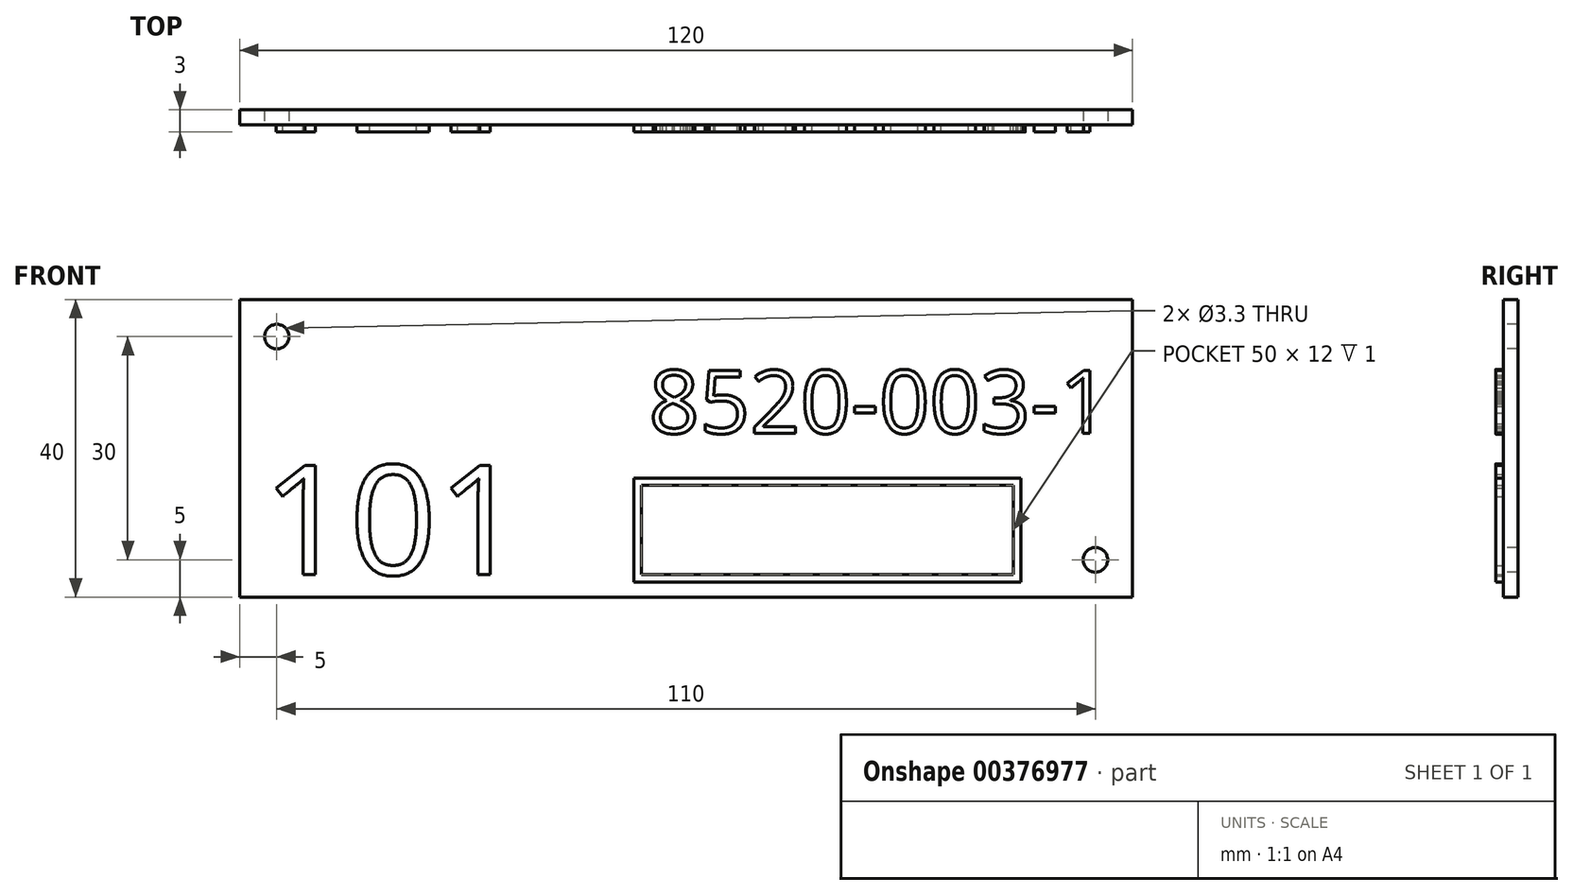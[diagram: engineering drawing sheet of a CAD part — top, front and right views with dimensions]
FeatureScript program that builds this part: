
annotation { "Feature Type Name" : "Feature", "Feature Type Description" : "" }
export const myFeature = defineFeature(function(context is Context, id is Id, definition is map)
    precondition{}
    {
        {
            var Q0;
            Q0=qCreatedBy(makeId("Front.planeOp"),FACE);
            var sketch = newSketch(context, id + "F0", { "sketchPlane" : qUnion([Q0])});
            skLineSegment(sketch, "E0.bottom", {"start": v(60, -20) * mm, "end": v(-60, -20) * mm});
            skLineSegment(sketch, "E0.top", {"start": v(60, 20) * mm, "end": v(-60, 20) * mm});
            skLineSegment(sketch, "E0.left", {"start": v(60, -20) * mm, "end": v(60, 20) * mm});
            skLineSegment(sketch, "E0.right", {"start": v(-60, -20) * mm, "end": v(-60, 20) * mm});
            skPoint(sketch, "E0.middle", {"position": v(0, 0) * mm});
            skSolve(sketch);
        }
        {
            var Q0;
            Q0=makeQuery(id+"F0.imprint","IMPRINT",FACE,{"disambiguationData":[TD([[makeQuery(id+"F0.imprint","IMPRINT",EDGE,{"derivedFrom":sQuery(id+"F0.wireOp",EDGE,"E0.bottom")}),-1.0]])]});
            extrude(context, id + "F1", {"entities" : qUnion([Q0]), "depth" : 2 * mm});
        }
        {
            var Q0;
            Q0=makeQuery(id+"F1.opExtrude","CAP_FACE",FACE,{"disambiguationData":[OSD([sQuery(id+"F0.wireOp",EDGE,"E0.bottom"),sQuery(id+"F0.wireOp",EDGE,"E0.top"),sQuery(id+"F0.wireOp",EDGE,"E0.left"),sQuery(id+"F0.wireOp",EDGE,"E0.right")])],"isStart":false});
            var sketch = newSketch(context, id + "F2", { "sketchPlane" : qUnion([Q0])});
            skPoint(sketch, "E1", {"position": v(-55, 15) * mm});
            skPoint(sketch, "E2", {"position": v(55, -15) * mm});
            skSolve(sketch);
        }
        {
            var Q0;
            Q0=sQuery(id+"F2.wireOp",VERTEX,"E1");
            var Q1;
            Q1=sQuery(id+"F2.wireOp",VERTEX,"E2");
            var Q2;
            Q2=makeQuery(id+"F1.opExtrude","SWEPT_BODY",BODY,{"disambiguationData":[OSD([sQuery(id+"F0.wireOp",EDGE,"E0.bottom"),sQuery(id+"F0.wireOp",EDGE,"E0.top"),sQuery(id+"F0.wireOp",EDGE,"E0.left"),sQuery(id+"F0.wireOp",EDGE,"E0.right")])]});
            hole(context, id + "F3", {"style" : HoleStyle.SIMPLE, "endStyle" : HoleEndStyle.THROUGH, "holeDiameter" : 3.3 * mm, "locations" : qUnion([Q0, Q1]), "scope" : qUnion([Q2]), "isTappedThrough" : true});
        }
        {
            var Q0;
            Q0=makeQuery(id+"F1.opExtrude","CAP_FACE",FACE,{"disambiguationData":[OSD([sQuery(id+"F0.wireOp",EDGE,"E0.bottom"),sQuery(id+"F0.wireOp",EDGE,"E0.top"),sQuery(id+"F0.wireOp",EDGE,"E0.left"),sQuery(id+"F0.wireOp",EDGE,"E0.right")])],"isStart":false});
            var sketch = newSketch(context, id + "F4", { "sketchPlane" : qUnion([Q0])});
            skText(sketch, "E3", { "text": "8520-003-1", "fontName": "OpenSans-Regular.ttf"});
            const initialGuessF4  = {"E3": [-0.005, 0.002, 1, 0, 0.00854]};
            skSetInitialGuess(sketch, initialGuessF4);
            skSolve(sketch);
        }
        {
            var Q0;
            Q0=qSketchRegion(id+"F4",true);
            extrude(context, id + "F5", {"entities" : qUnion([Q0]), "operationType" : NewBodyOperationType.ADD, "depth" : 1 * mm});
        }
        {
            var Q0;
            {var subQ0=sQuery(id+"F0.wireOp",EDGE,"E0.top");var subQ1=sQuery(id+"F0.wireOp",EDGE,"E0.left");var subQ2=sQuery(id+"F0.wireOp",EDGE,"E0.right");var subQ3=sQuery(id+"F0.wireOp",EDGE,"E0.bottom");Q0=makeQuery(id+"F5.boolean.opBoolean","SPLIT",FACE,{"disambiguationData":[TD([makeQuery(id+"F1.opExtrude","SWEPT_FACE",FACE,{"disambiguationData":[OSD([subQ3])]})])],"derivedFrom":makeQuery(id+"F1.opExtrude","CAP_FACE",FACE,{"disambiguationData":[OSD([subQ3,subQ0,subQ1,subQ2])],"isStart":false})});}
            var sketch = newSketch(context, id + "F6", { "sketchPlane" : qUnion([Q0])});
            skText(sketch, "E4", { "text": "101", "fontName": "OpenSans-Regular.ttf"});
            const initialGuessF6  = {"E4": [-0.057, -0.017, 1, 0, 0.0148]};
            skSetInitialGuess(sketch, initialGuessF6);
            skSolve(sketch);
        }
        {
            var Q0;
            Q0=qSketchRegion(id+"F6",true);
            extrude(context, id + "F7", {"entities" : qUnion([Q0]), "operationType" : NewBodyOperationType.ADD, "depth" : 1 * mm});
        }
        {
            var Q0;
            {var subQ46=sQuery(id+"F0.wireOp",EDGE,"E0.top");var subQ48=sQuery(id+"F0.wireOp",EDGE,"E0.left");var subQ66=sQuery(id+"F0.wireOp",EDGE,"E0.right");var subQ76=sQuery(id+"F0.wireOp",EDGE,"E0.bottom");var subQ77=makeQuery(id+"F1.opExtrude","SWEPT_FACE",FACE,{"disambiguationData":[OSD([subQ76])]});Q0=makeQuery(id+"F7.boolean.opBoolean","SPLIT",FACE,{"disambiguationData":[TD([subQ77])],"derivedFrom":makeQuery(id+"F5.boolean.opBoolean","SPLIT",FACE,{"disambiguationData":[TD([subQ77])],"derivedFrom":makeQuery(id+"F1.opExtrude","CAP_FACE",FACE,{"disambiguationData":[OSD([subQ76,subQ46,subQ48,subQ66])],"isStart":false})})});}
            var sketch = newSketch(context, id + "F8", { "sketchPlane" : qUnion([Q0])});
            skLineSegment(sketch, "E5.bottom", {"start": v(45, -18) * mm, "end": v(-7, -18) * mm});
            skLineSegment(sketch, "E5.top", {"start": v(45, -4) * mm, "end": v(-7, -4) * mm});
            skLineSegment(sketch, "E5.left", {"start": v(45, -18) * mm, "end": v(45, -4) * mm});
            skLineSegment(sketch, "E5.right", {"start": v(-7, -18) * mm, "end": v(-7, -4) * mm});
            skPoint(sketch, "E5.middle", {"position": v(19, -11) * mm});
            skLineSegment(sketch, "E6.0", {"start": v(44, -5) * mm, "end": v(-6, -5) * mm});
            skLineSegment(sketch, "E6.1", {"start": v(44, -17) * mm, "end": v(44, -5) * mm});
            skLineSegment(sketch, "E6.2", {"start": v(44, -17) * mm, "end": v(-6, -17) * mm});
            skLineSegment(sketch, "E6.3", {"start": v(-6, -17) * mm, "end": v(-6, -5) * mm});
            skSolve(sketch);
        }
        {
            var Q0;
            Q0=makeQuery(id+"F8.imprint","IMPRINT",FACE,{"disambiguationData":[TD([[makeQuery(id+"F8.imprint","IMPRINT",EDGE,{"derivedFrom":sQuery(id+"F8.wireOp",EDGE,"E5.bottom")}),-1.0]])]});
            extrude(context, id + "F9", {"entities" : qUnion([Q0]), "operationType" : NewBodyOperationType.ADD, "depth" : 1 * mm});
        }
    });
